FCSTD DOCUMENT  (FreeCAD 1.0R39319 (Git))
Label: 123Unnamed1
License: All rights reserved
LicenseURL: https://en.wikipedia.org/wiki/All_rights_reserved
objects: Sketcher::SketchObject×1, PartDesign::Body×1
note: 3 computed .brp shape members not serialized (recipe doc carries the construction recipe); baked Part::Feature solids carry a one-line shape summary decoded from their .brp

FEATURE [Sketcher::SketchObject] Sketch
  ArcFitTolerance = 1e-06
  AttachmentSupport = -> [XY_Plane]
  FullyConstrained = false
  MakeInternals = false
  MapMode = 5
  sketch-geometry (8):
    g0: LineSegment StartX=0 StartY=0 StartZ=0 EndX=26.5 EndY=0 EndZ=0
    g1: LineSegment StartX=26.5 StartY=0 StartZ=0 EndX=26.5 EndY=26.5 EndZ=0
    g2: LineSegment StartX=26.5 StartY=26.5 StartZ=0 EndX=0 EndY=26.5 EndZ=0
    g3: LineSegment StartX=0 StartY=26.5 StartZ=0 EndX=0 EndY=0 EndZ=0
    g4: LineSegment StartX=5.09415 StartY=0 StartZ=0 EndX=21.5941 EndY=0 EndZ=0
    g5: LineSegment StartX=21.5941 StartY=0 StartZ=0 EndX=21.5941 EndY=16.5 EndZ=0
    g6: LineSegment StartX=21.5941 StartY=16.5 StartZ=0 EndX=5.09415 EndY=16.5 EndZ=0
    g7: LineSegment StartX=5.09415 StartY=16.5 StartZ=0 EndX=5.09415 EndY=0 EndZ=0
  constraints (22):
    c: Coincident(g0,g1)
    c: Coincident(g1,g2)
    c: Coincident(g2,g3)
    c: Coincident(g3,g0)
    c: Horizontal(g0)
    c: Horizontal(g2)
    c: Vertical(g1)
    c: Vertical(g3)
    c: Distance(g1,g3) = 26.5
    c: Distance(g0,g2) = 26.5
    c: Coincident(g0,g-1)
    c: Coincident(g4,g5)
    c: Coincident(g5,g6)
    c: Coincident(g6,g7)
    c: Coincident(g7,g4)
    c: Horizontal(g4)
    c: Horizontal(g6)
    c: Vertical(g5)
    c: Vertical(g7)
    c: Distance(g5,g7) = 16.5
    c: Distance(g4,g6) = 16.5
    c: PointOnObject(g4,g0)
FEATURE [PartDesign::Body] Body
  AllowCompound = false
  Group = -> [Sketch]
  Origin = -> Origin
